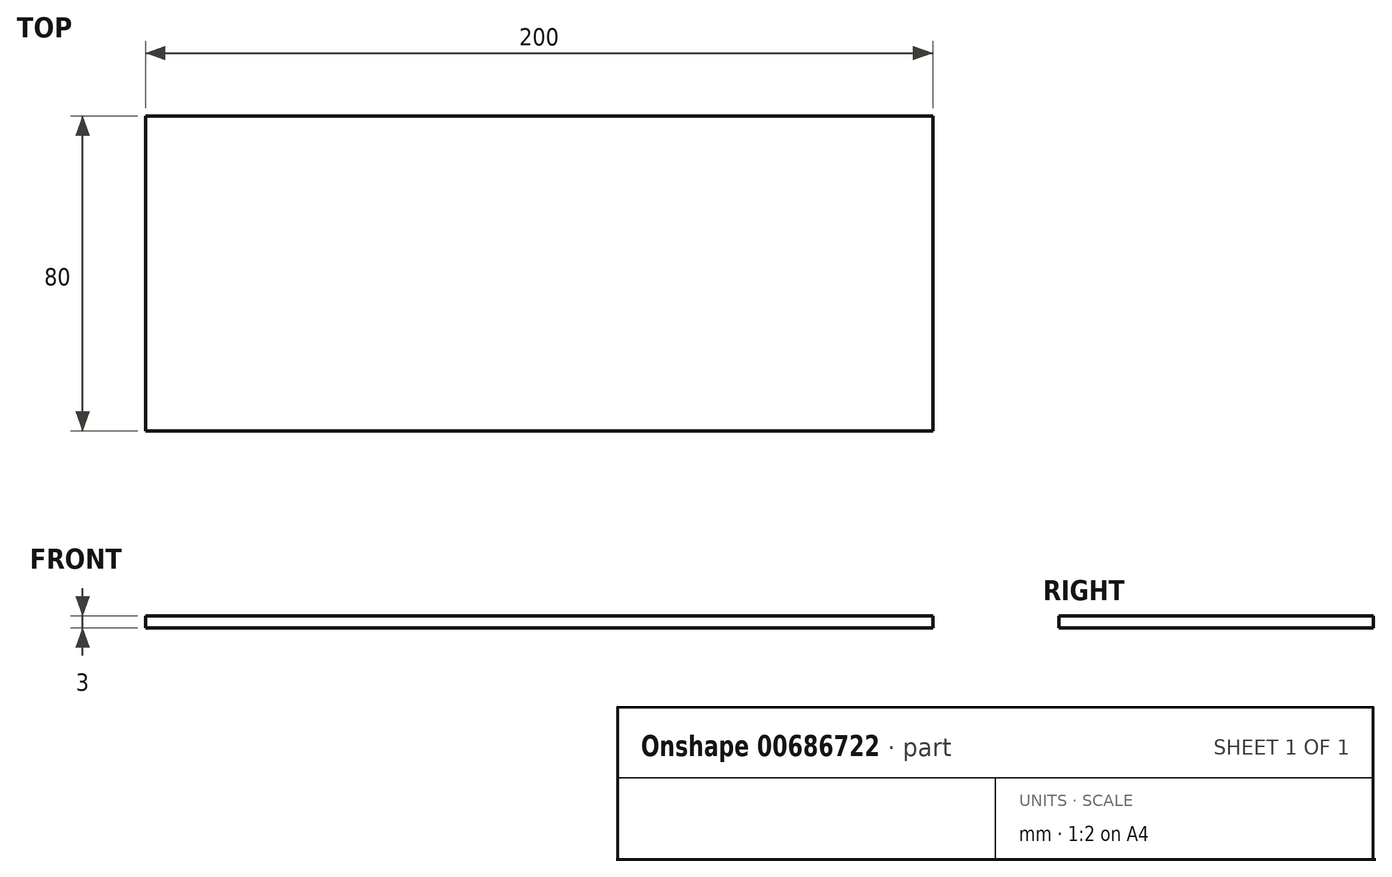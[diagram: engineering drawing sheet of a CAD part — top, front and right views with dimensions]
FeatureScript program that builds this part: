
annotation { "Feature Type Name" : "Feature", "Feature Type Description" : "" }
export const myFeature = defineFeature(function(context is Context, id is Id, definition is map)
    precondition{}
    {
        {
            var Q0;
            Q0=qCreatedBy(makeId("Top.planeOp"),FACE);
            var sketch = newSketch(context, id + "F0", { "sketchPlane" : qUnion([Q0])});
            skLineSegment(sketch, "E0.bottom", {"start": v(0, 0) * mm, "end": v(200, 0) * mm});
            skLineSegment(sketch, "E0.top", {"start": v(0, 80) * mm, "end": v(200, 80) * mm});
            skLineSegment(sketch, "E0.left", {"start": v(0, 0) * mm, "end": v(0, 80) * mm});
            skLineSegment(sketch, "E0.right", {"start": v(200, 0) * mm, "end": v(200, 80) * mm});
            skSolve(sketch);
        }
        {
            var Q0;
            Q0=makeQuery(id+"F0.imprint","IMPRINT",FACE,{"disambiguationData":[TD([[makeQuery(id+"F0.imprint","IMPRINT",EDGE,{"derivedFrom":sQuery(id+"F0.wireOp",EDGE,"E0.bottom")}),1.0]])]});
            extrude(context, id + "F1", {"entities" : qUnion([Q0]), "depth" : 3 * mm, "offsetDistance" : 25 * mm});
        }
    });
